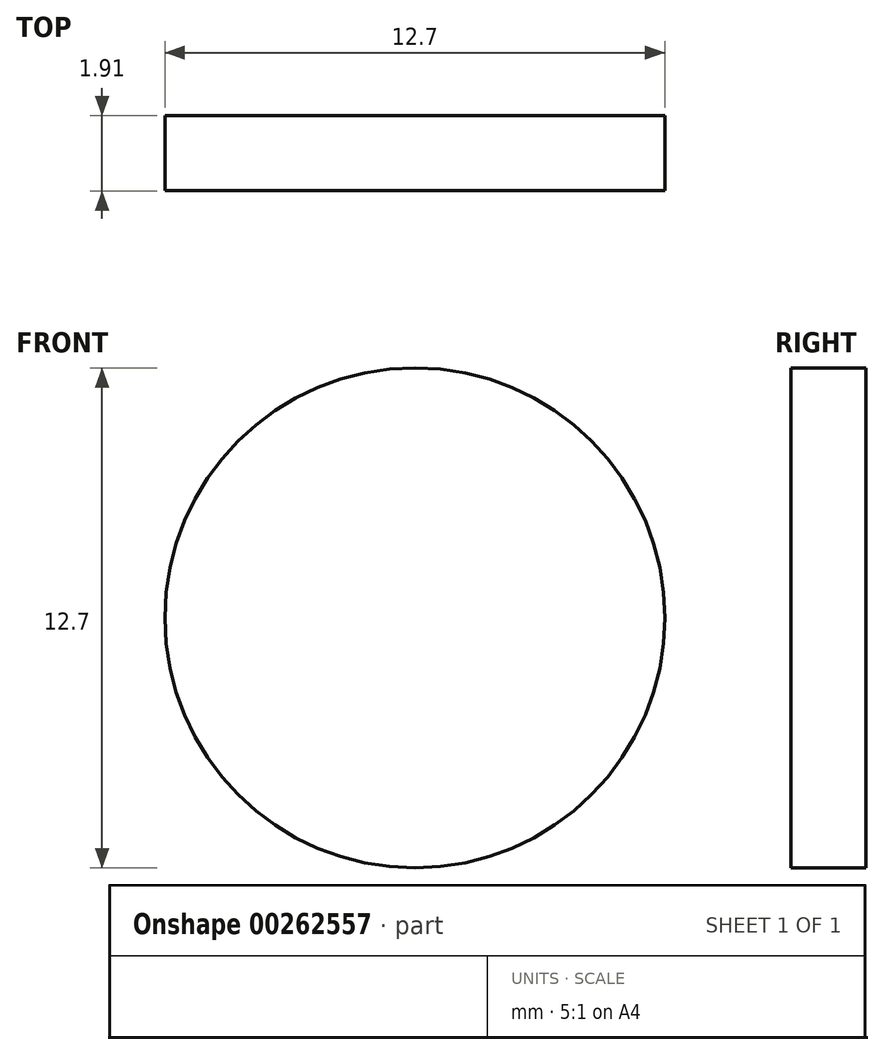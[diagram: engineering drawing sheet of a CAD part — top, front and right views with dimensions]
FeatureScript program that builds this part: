
annotation { "Feature Type Name" : "Feature", "Feature Type Description" : "" }
export const myFeature = defineFeature(function(context is Context, id is Id, definition is map)
    precondition{}
    {
        {
            var Q0;
            Q0=qCreatedBy(makeId("Front.planeOp"),FACE);
            var sketch = newSketch(context, id + "F0", { "sketchPlane" : qUnion([Q0])});
            skCircle(sketch, "E0", {"center": v(0, 0) * mm, "radius": 6.35 * mm});
            skSolve(sketch);
        }
        {
            var Q0;
            Q0 = qSketchRegion(id + "F0", true);
            extrude(context, id + "F1", {"entities" : qUnion([Q0]), "depth" : 1.9 * mm});
        }
    });
